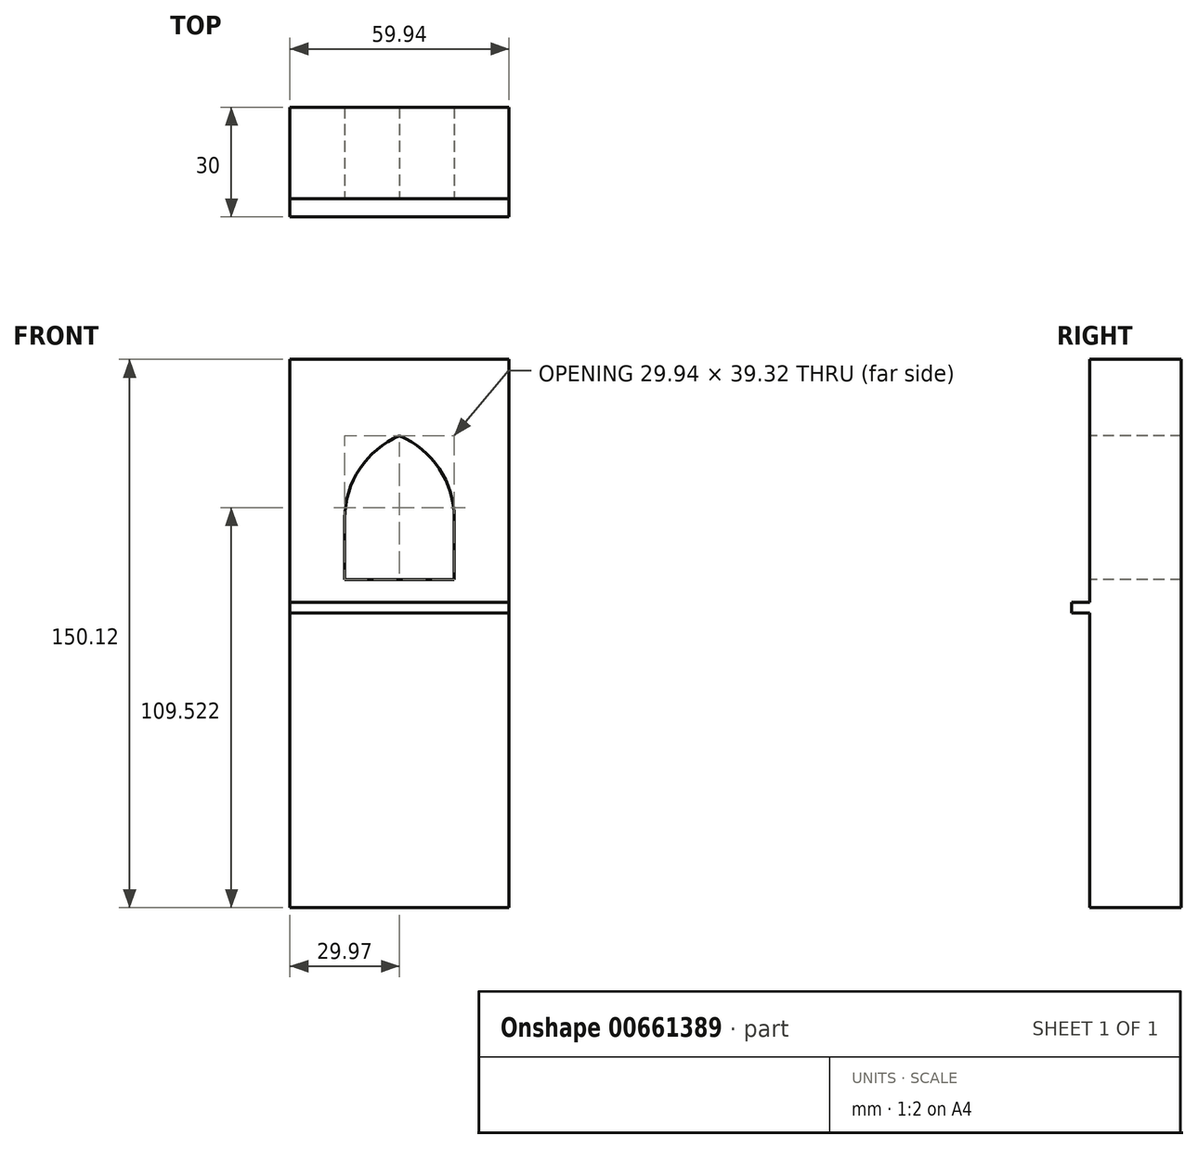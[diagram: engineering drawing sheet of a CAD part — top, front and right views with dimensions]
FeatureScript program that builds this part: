
annotation { "Feature Type Name" : "Feature", "Feature Type Description" : "" }
export const myFeature = defineFeature(function(context is Context, id is Id, definition is map)
    precondition{}
    {
        {
            var Q0;
            Q0=qCreatedBy(makeId("Front.planeOp"),FACE);
            var sketch = newSketch(context, id + "F0", { "sketchPlane" : qUnion([Q0])});
            skLineSegment(sketch, "E0.bottom", {"start": v(29.97, -75.06) * mm, "end": v(-29.97, -75.06) * mm});
            skLineSegment(sketch, "E0.top", {"start": v(29.97, 75.06) * mm, "end": v(-29.97, 75.06) * mm});
            skLineSegment(sketch, "E0.left", {"start": v(29.97, -75.06) * mm, "end": v(29.97, 75.06) * mm});
            skLineSegment(sketch, "E0.right", {"start": v(-29.97, -75.06) * mm, "end": v(-29.97, 75.06) * mm});
            skPoint(sketch, "E0.middle", {"position": v(0, 0) * mm});
            skSolve(sketch);
        }
        {
            var Q0;
            Q0=makeQuery(id+"F0.imprint","IMPRINT",FACE,{"disambiguationData":[TD([[makeQuery(id+"F0.imprint","IMPRINT",EDGE,{"derivedFrom":sQuery(id+"F0.wireOp",EDGE,"E0.bottom")}),-1.0]])]});
            extrude(context, id + "F1", {"entities" : qUnion([Q0]), "depth" : 25 * mm, "offsetDistance" : 25 * mm});
        }
        {
            var Q0;
            Q0=makeQuery(id+"F1.opExtrude","CAP_FACE",FACE,{"disambiguationData":[OSD([sQuery(id+"F0.wireOp",EDGE,"E0.bottom"),sQuery(id+"F0.wireOp",EDGE,"E0.top"),sQuery(id+"F0.wireOp",EDGE,"E0.left"),sQuery(id+"F0.wireOp",EDGE,"E0.right")])],"isStart":false});
            var sketch = newSketch(context, id + "F2", { "sketchPlane" : qUnion([Q0])});
            skLineSegment(sketch, "E1", {"start": v(-29.97, 14.8) * mm, "end": v(-14.97, 14.8) * mm});
            skLineSegment(sketch, "E2", {"start": v(-14.97, 14.8) * mm, "end": v(14.97, 14.8) * mm});
            skLineSegment(sketch, "E3", {"start": v(14.97, 14.8) * mm, "end": v(29.97, 14.8) * mm});
            skLineSegment(sketch, "E4", {"start": v(-14.97, 14.8) * mm, "end": v(-14.97, 31.56) * mm});
            skLineSegment(sketch, "E5", {"start": v(14.97, 14.8) * mm, "end": v(14.97, 31.56) * mm});
            skLineSegment(sketch, "E6", {"start": v(14.97, 31.56) * mm, "end": v(-14.97, 31.56) * mm});
            skArc(sketch, "E7", {"start": v(0, 54.12) * mm, "mid": v(-10.89, 45.1) * mm, "end": v(-14.97, 31.56) * mm});
            skArc(sketch, "E8", {"start": v(14.97, 31.56) * mm, "mid": v(10.89, 45.1) * mm, "end": v(0, 54.12) * mm});
            skSolve(sketch);
        }
        {
            var Q0;
            Q0=makeQuery(id+"F2.imprint","IMPRINT",FACE,{"disambiguationData":[TD([[makeQuery(id+"F2.imprint","IMPRINT",EDGE,{"derivedFrom":sQuery(id+"F2.wireOp",EDGE,"E6")}),-1.0]])]});
            var Q1;
            Q1=makeQuery(id+"F2.imprint","IMPRINT",FACE,{"disambiguationData":[TD([[makeQuery(id+"F2.imprint","IMPRINT",EDGE,{"derivedFrom":sQuery(id+"F2.wireOp",EDGE,"E2")}),1.0]])]});
            extrude(context, id + "F3", {"entities" : qUnion([Q0, Q1]), "operationType" : NewBodyOperationType.REMOVE, "oppositeDirection" : true, "depth" : 31 * mm, "offsetDistance" : 25 * mm});
        }
        {
            var Q0;
            Q0=makeQuery(id+"F1.opExtrude","CAP_FACE",FACE,{"disambiguationData":[OSD([sQuery(id+"F0.wireOp",EDGE,"E0.bottom"),sQuery(id+"F0.wireOp",EDGE,"E0.top"),sQuery(id+"F0.wireOp",EDGE,"E0.left"),sQuery(id+"F0.wireOp",EDGE,"E0.right")])],"isStart":false});
            var sketch = newSketch(context, id + "F4", { "sketchPlane" : qUnion([Q0])});
            skLineSegment(sketch, "E9", {"start": v(-29.97, 8.6) * mm, "end": v(29.97, 8.6) * mm});
            skLineSegment(sketch, "E10", {"start": v(29.97, 8.6) * mm, "end": v(29.97, 5.67) * mm});
            skLineSegment(sketch, "E11", {"start": v(29.97, 5.67) * mm, "end": v(-29.97, 5.67) * mm});
            skLineSegment(sketch, "E12", {"start": v(-29.97, 5.67) * mm, "end": v(-29.97, 8.6) * mm});
            skSolve(sketch);
        }
        {
            var Q0;
            Q0=makeQuery(id+"F4.imprint","IMPRINT",FACE,{"disambiguationData":[TD([[makeQuery(id+"F4.imprint","IMPRINT",EDGE,{"derivedFrom":sQuery(id+"F4.wireOp",EDGE,"E9")}),-1.0]])]});
            extrude(context, id + "F5", {"entities" : qUnion([Q0]), "operationType" : NewBodyOperationType.ADD, "depth" : 5 * mm, "offsetDistance" : 25 * mm});
        }
    });
